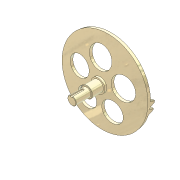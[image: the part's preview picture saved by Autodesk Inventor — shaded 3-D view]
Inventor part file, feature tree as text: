
AUTODESK INVENTOR PART (.ipt)
format: ipt  version: unknown  size: 615,424 bytes
history: native  units: mm (DEFAULTED — no unit token found)
features: sketch x6, extrude x5, fillet x3, pattern_circular x3, revolve x1, plane x1, chamfer x1
ambient origin geometry x8: Origin, YZ Plane, XZ Plane, XY Plane, X Axis, Y Axis, Z Axis, Center Point
feature tree (20):
  revolve  "Revolution3"  [1 undecoded]
  plane  "Work Plane11"
  sketch  "Sketch38"  dims[d153=60.0mm]
  chamfer  "Chamfer3"  Distance=16.0mm
  extrude  "Extrusion33"  Depth=20.0mm
  fillet  "Fillet5"  Radius=10.0mm
  extrude  "Extrusion34"  Depth=8.0mm
  pattern_circular  "Circular Pattern3"  [2 undecoded]
  extrude  "Extrusion38"  Depth=11.0mm
  extrude  "Extrusion39"  TaperAngle=90.0deg  [1 undecoded]
  pattern_circular  "Circular Pattern6"  Count=6  [1 undecoded]
  pattern_circular  "Circular Pattern7"  [2 undecoded]
  fillet  "Fillet6"  Radius=3.6mm
  fillet  "Fillet7"  Radius=4.71mm
  extrude  "Extrusion40"  Depth=3.490659mm
  sketch  "Sketch37"  dims[d43=60.0mm d46=60.0mm]
  sketch  "Sketch41"  dims[d154=4.0mm]
  sketch  "Sketch42"  dims[d155=4.0mm]
  sketch  "Sketch46"  dims[d156=0.0mm]
  sketch  "Sketch47"  dims[d157=3.0mm d158=16.0mm d159=20.0mm d160=10.0mm d161=8.0mm d162=6.0mm d163=11.0mm d164=90.0deg d165=60.0mm d166=3.0mm d167=3.6mm d168=4.71mm d169=3.490659mm d170=2.355mm d182=0.5mm d183=2.0mm d184=45.0deg d185=3.0mm d186=1.5mm d187=4.5mm d188=16.0mm d189=0.0mm d190=1.5mm d191=30.0mm d192=32.0mm d193=16.0mm d194=0.0mm d195=50.0mm d196=360.0deg d213=4.0mm d214=1.745329mm d215=3.490659mm d216=7.0mm d217=0.0mm d218=7.0mm d219=0.0mm d220=30.0mm d221=3.141593mm d223=20.0mm d224=43.633231mm d226=0.5mm d227=0.5mm d228=0.1mm d229=0.0mm]
note: 7 required parameter values undecoded (feature->parameter linkage not recoverable at this tier; creation-order binding heuristic only, values carry confidence <= 0.55)